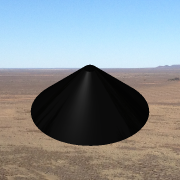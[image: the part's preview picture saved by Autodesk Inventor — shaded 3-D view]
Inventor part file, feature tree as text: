
AUTODESK INVENTOR PART (.ipt)
format: ipt  version: 2013 SP2 (Build 170200200, 200)  size: 152,064 bytes
history: native  units: in
note: dims shown in document units (in); Inventor stores cm internally (conversion verified against a paired STEP export)
features: sketch x2, revolve x1, extrude x1
ambient origin geometry x8: Origin, YZ Plane, XZ Plane, XY Plane, X Axis, Y Axis, Z Axis, Center Point
bodies: Solid1 (feature_tree)
feature tree (4):
  revolve  "Revolution2"  [1 undecoded]
  extrude  "Extrusion3"  [1 undecoded]
  sketch  "Sketch6"  dims[d11=90.0deg d12=1.0in]
  sketch  "Sketch7"  dims[d13=30.0in d14=0.0in]
note: 2 required parameter values undecoded (feature->parameter linkage not recoverable at this tier; creation-order binding heuristic only, values carry confidence <= 0.55)